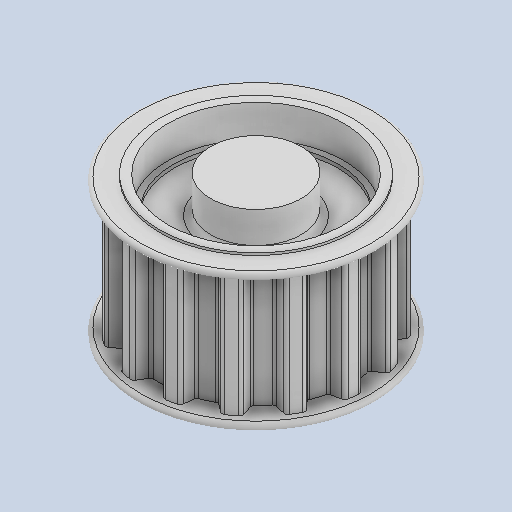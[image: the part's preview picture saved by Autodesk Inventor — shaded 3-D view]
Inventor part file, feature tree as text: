
AUTODESK INVENTOR PART (.ipt)
format: ipt  version: 2022 (Build 260153000, 153)  size: 369,152 bytes
history: native  units: in
note: dims shown in document units (in); Inventor stores cm internally (conversion verified against a paired STEP export)
features: fillet x1
ambient origin geometry x8: Origin, YZ Plane, XZ Plane, XY Plane, X Axis, Y Axis, Z Axis, Center Point
bodies: Solid1 (feature_tree)
feature tree (1):
  fillet  "Fillet1"  [1 undecoded]
note: 1 required parameter value undecoded (feature->parameter linkage not recoverable at this tier; creation-order binding heuristic only, values carry confidence <= 0.55)
